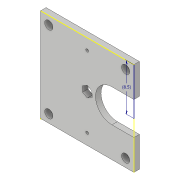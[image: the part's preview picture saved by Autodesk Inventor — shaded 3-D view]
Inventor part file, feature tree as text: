
AUTODESK INVENTOR PART (.ipt)
format: ipt  version: 2019 (Build 230136000, 136)  size: 158,208 bytes
history: native  units: mm
features: sketch x9, extrude x8
ambient origin geometry x8: Origin, YZ Plane, XZ Plane, XY Plane, X Axis, Y Axis, Z Axis, Center Point
bodies: Solid1 (feature_tree)
feature tree (17):
  extrude  "Extrusion1"  Depth=170.0mm
  extrude  "Extrusion2"  Depth=10.0mm
  extrude  "Extrusion3"  Depth=155.0mm
  extrude  "Extrusion4"  Depth=140.0mm
  sketch  "Sketch5"  dims[d9=140.0mm d10=15.0mm]
  extrude  "Extrusion5"  Depth=15.0mm
  extrude  "Extrusion6"  Depth=15.0mm
  extrude  "Extrusion7"  Depth=10.0mm TaperAngle=0.0deg
  extrude  "Extrusion8"  Depth=85.0mm
  sketch  "Sketch1"  dims[d0=170.0mm d1=170.0mm]
  sketch  "Sketch2"  dims[d2=10.0mm d3=0.0mm d4=15.0mm]
  sketch  "Sketch3"  dims[d5=15.0mm d6=155.0mm]
  sketch  "Sketch4"  dims[d7=140.0mm d8=140.0mm]
  sketch  "Sketch6"  dims[d11=15.0mm d12=15.0mm]
  sketch  "Sketch7"  dims[d13=15.0mm d14=10.0mm d15=0.0mm]
  sketch  "Sketch8"  dims[d16=85.0mm d17=85.0mm]
  sketch  "Sketch9"  dims[d18=10.0mm d19=10.0mm d20=0.0mm d21=85.0mm d22=20.0mm d23=130.0mm d24=5.0mm d25=5.0mm d26=10.0mm d27=0.0mm d28=85.0mm d29=40.0mm d30=60.0mm d31=10.0mm d32=0.0mm d33=30.0mm d34=60.0mm d35=10.0mm d36=0.0mm d37=10.0mm d38=0.0mm d39=10.0mm d40=0.0mm]
